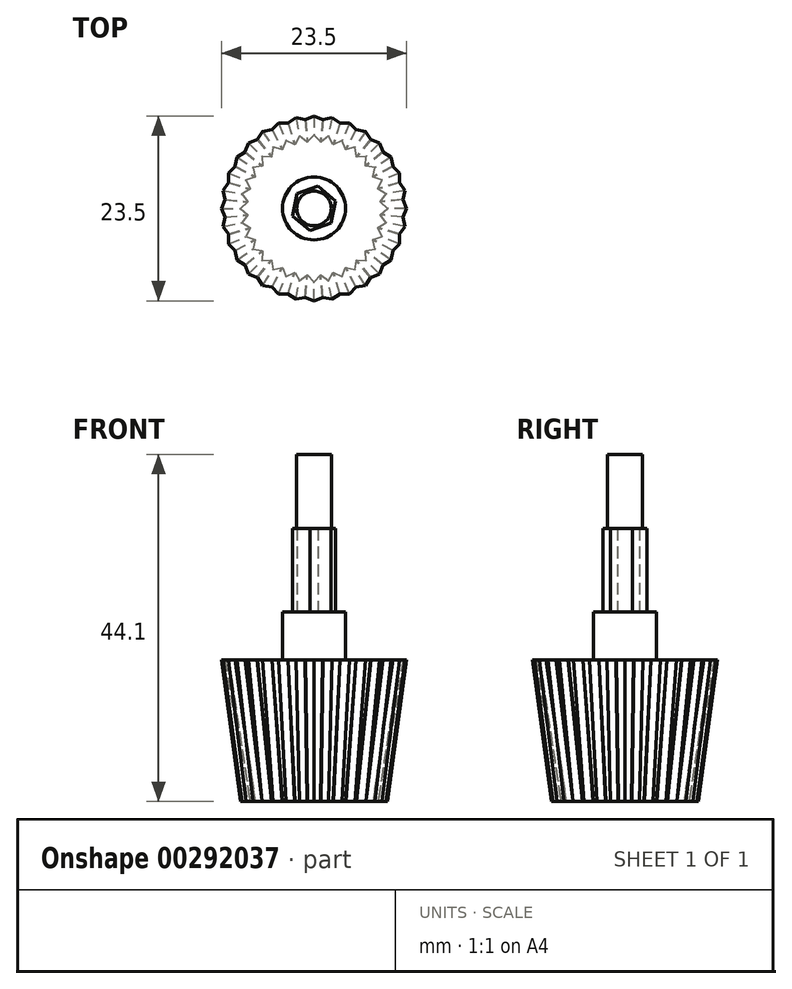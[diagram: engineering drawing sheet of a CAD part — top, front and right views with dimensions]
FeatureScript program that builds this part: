
annotation { "Feature Type Name" : "Feature", "Feature Type Description" : "" }
export const myFeature = defineFeature(function(context is Context, id is Id, definition is map)
    precondition{}
    {
        {
            var Q0;
            Q0=qCreatedBy(makeId("Top.planeOp"),FACE);
            var sketch = newSketch(context, id + "F0", { "sketchPlane" : qUnion([Q0])});
            skCircle(sketch, "E0", {"center": v(0, 0) * mm, "radius": 8.5 * mm});
            skSolve(sketch);
        }
        {
            var Q0;
            Q0 = qSketchRegion(id + "F0", true);
            extrude(context, id + "F1", {"entities" : qUnion([Q0]), "depth" : 18 * mm, "hasDraft" : true, "draftAngle" : 9 * degree});
        }
        {
            var Q0;
            Q0=makeQuery(id+"F1.opExtrude","CAP_FACE",FACE,{"disambiguationData":[OSD([sQuery(id+"F0.wireOp",EDGE,"E0")])],"isStart":false});
            var sketch = newSketch(context, id + "F2", { "sketchPlane" : qUnion([Q0])});
            skLineSegment(sketch, "E1", {"start": v(-1.1, 11.3) * mm, "end": v(0, 11.75) * mm});
            skLineSegment(sketch, "E2", {"start": v(0, 11.75) * mm, "end": v(1.1, 11.3) * mm});
            skLineSegment(sketch, "E3", {"start": v(1.1, 11.3) * mm, "end": v(-1.1, 11.3) * mm});
            skSolve(sketch);
        }
        {
            var Q0;
            Q0=makeQuery(id+"F1.opExtrude","CAP_FACE",FACE,{"disambiguationData":[OSD([sQuery(id+"F0.wireOp",EDGE,"E0")])],"isStart":true});
            var sketch = newSketch(context, id + "F3", { "sketchPlane" : qUnion([Q0])});
            skLineSegment(sketch, "E4", {"start": v(0.8, -8.46) * mm, "end": v(0, -9.34) * mm});
            skLineSegment(sketch, "E5", {"start": v(0, -9.34) * mm, "end": v(-0.8, -8.46) * mm});
            skLineSegment(sketch, "E6", {"start": v(-0.8, -8.46) * mm, "end": v(0.8, -8.46) * mm});
            skSolve(sketch);
        }
        {
            var Q0;
            Q0 = qSketchRegion(id + "F2", true);
            var Q1;
            Q1 = qSketchRegion(id + "F3", true);
            var Q2;
            {var subQ0=sQuery(id+"F2.wireOp",EDGE,"E1");Q2=makeQuery(id+"F2.imprint","IMPRINT",FACE,{"disambiguationData":[TD([[makeQuery(id+"F2.imprint","IMPRINT",EDGE,{"derivedFrom":subQ0}),-1.0]])]});}
            var Q3;
            {var subQ0=sQuery(id+"F3.wireOp",EDGE,"E4");Q3=makeQuery(id+"F3.imprint","IMPRINT",FACE,{"disambiguationData":[TD([[makeQuery(id+"F3.imprint","IMPRINT",EDGE,{"derivedFrom":subQ0}),-1.0]])]});}
            loft(context, id + "F4", {"sheetProfilesArray" : [{ "sheetProfileEntities" : qUnion([Q0]) }, { "sheetProfileEntities" : qUnion([Q1]) }], "wireProfilesArray" : [{ "wireProfileEntities" : qUnion([Q2]) }, { "wireProfileEntities" : qUnion([Q3]) }]});
        }
        {
            var Q0;
            {var subQ0=sQuery(id+"F3.wireOp",EDGE,"E4");var subQ5=sQuery(id+"F2.wireOp",EDGE,"E1");Q0=makeQuery(id+"F4.opLoft","SWEPT_BODY",BODY,{"disambiguationData":[OSD([makeQuery(id+"F2.imprint","IMPRINT",FACE,{"disambiguationData":[TD([[makeQuery(id+"F2.imprint","IMPRINT",EDGE,{"derivedFrom":subQ5}),-1.0]])]}),makeQuery(id+"F3.imprint","IMPRINT",FACE,{"disambiguationData":[TD([[makeQuery(id+"F3.imprint","IMPRINT",EDGE,{"derivedFrom":subQ0}),-1.0]])]})])]});}
            var Q1;
            Q1=makeQuery(id+"F1.opExtrude","CAP_EDGE",EDGE,{"disambiguationData":[OSD([sQuery(id+"F0.wireOp",EDGE,"E0")])],"isStart":true});
            circularPattern(context, id + "F5", {"operationType" : NewBodyOperationType.ADD, "entities" : qUnion([Q0]), "axis" : qUnion([Q1]), "angle" : 360 * degree, "instanceCount" : 32, "equalSpace" : true});
        }
        {
            var Q0;
            {var subQ0=sQuery(id+"F2.wireOp",EDGE,"E3");var subQ1=sQuery(id+"F0.wireOp",EDGE,"E0");var subQ3=makeQuery(id+"F4.opLoft","CAP_FACE",FACE,{"disambiguationData":[OSD([makeQuery(id+"F2.imprint","IMPRINT",FACE,{"disambiguationData":[TD([[makeQuery(id+"F2.imprint","IMPRINT",EDGE,{"derivedFrom":subQ0}),-1.0]])]})])],"isStart":true});Q0=makeQuery(id+"F5.boolean.opBoolean","MERGE",FACE,{"derivedFrom":[makeQuery(id+"F1.opExtrude","CAP_FACE",FACE,{"disambiguationData":[OSD([subQ1])],"isStart":false}),subQ3,makeQuery(id+"F5.opPattern","COPY",FACE,{"derivedFrom":subQ3,"instanceName":"1"}),makeQuery(id+"F5.opPattern","COPY",FACE,{"derivedFrom":subQ3,"instanceName":"2"}),makeQuery(id+"F5.opPattern","COPY",FACE,{"derivedFrom":subQ3,"instanceName":"3"}),makeQuery(id+"F5.opPattern","COPY",FACE,{"derivedFrom":subQ3,"instanceName":"4"}),makeQuery(id+"F5.opPattern","COPY",FACE,{"derivedFrom":subQ3,"instanceName":"5"}),makeQuery(id+"F5.opPattern","COPY",FACE,{"derivedFrom":subQ3,"instanceName":"6"}),makeQuery(id+"F5.opPattern","COPY",FACE,{"derivedFrom":subQ3,"instanceName":"7"}),makeQuery(id+"F5.opPattern","COPY",FACE,{"derivedFrom":subQ3,"instanceName":"8"}),makeQuery(id+"F5.opPattern","COPY",FACE,{"derivedFrom":subQ3,"instanceName":"9"}),makeQuery(id+"F5.opPattern","COPY",FACE,{"derivedFrom":subQ3,"instanceName":"10"}),makeQuery(id+"F5.opPattern","COPY",FACE,{"derivedFrom":subQ3,"instanceName":"11"}),makeQuery(id+"F5.opPattern","COPY",FACE,{"derivedFrom":subQ3,"instanceName":"12"}),makeQuery(id+"F5.opPattern","COPY",FACE,{"derivedFrom":subQ3,"instanceName":"13"}),makeQuery(id+"F5.opPattern","COPY",FACE,{"derivedFrom":subQ3,"instanceName":"14"}),makeQuery(id+"F5.opPattern","COPY",FACE,{"derivedFrom":subQ3,"instanceName":"15"}),makeQuery(id+"F5.opPattern","COPY",FACE,{"derivedFrom":subQ3,"instanceName":"16"}),makeQuery(id+"F5.opPattern","COPY",FACE,{"derivedFrom":subQ3,"instanceName":"17"}),makeQuery(id+"F5.opPattern","COPY",FACE,{"derivedFrom":subQ3,"instanceName":"18"}),makeQuery(id+"F5.opPattern","COPY",FACE,{"derivedFrom":subQ3,"instanceName":"19"}),makeQuery(id+"F5.opPattern","COPY",FACE,{"derivedFrom":subQ3,"instanceName":"20"}),makeQuery(id+"F5.opPattern","COPY",FACE,{"derivedFrom":subQ3,"instanceName":"21"}),makeQuery(id+"F5.opPattern","COPY",FACE,{"derivedFrom":subQ3,"instanceName":"22"}),makeQuery(id+"F5.opPattern","COPY",FACE,{"derivedFrom":subQ3,"instanceName":"23"}),makeQuery(id+"F5.opPattern","COPY",FACE,{"derivedFrom":subQ3,"instanceName":"24"}),makeQuery(id+"F5.opPattern","COPY",FACE,{"derivedFrom":subQ3,"instanceName":"25"}),makeQuery(id+"F5.opPattern","COPY",FACE,{"derivedFrom":subQ3,"instanceName":"26"}),makeQuery(id+"F5.opPattern","COPY",FACE,{"derivedFrom":subQ3,"instanceName":"27"}),makeQuery(id+"F5.opPattern","COPY",FACE,{"derivedFrom":subQ3,"instanceName":"28"}),makeQuery(id+"F5.opPattern","COPY",FACE,{"derivedFrom":subQ3,"instanceName":"29"}),makeQuery(id+"F5.opPattern","COPY",FACE,{"derivedFrom":subQ3,"instanceName":"30"}),makeQuery(id+"F5.opPattern","COPY",FACE,{"derivedFrom":subQ3,"instanceName":"31"})]});}
            var sketch = newSketch(context, id + "F6", { "sketchPlane" : qUnion([Q0])});
            skCircle(sketch, "E7", {"center": v(0, 0) * mm, "radius": 4 * mm});
            skSolve(sketch);
        }
        {
            var Q0;
            Q0 = qSketchRegion(id + "F6", true);
            extrude(context, id + "F7", {"entities" : qUnion([Q0]), "operationType" : NewBodyOperationType.ADD, "depth" : 6.1 * mm});
        }
        {
            var Q0;
            Q0=makeQuery(id+"F7.opExtrude","CAP_FACE",FACE,{"disambiguationData":[OSD([sQuery(id+"F6.wireOp",EDGE,"E7")])],"isStart":false});
            var sketch = newSketch(context, id + "F8", { "sketchPlane" : qUnion([Q0])});
            skCircle(sketch, "E8.cCircle", {"center": v(0, 0) * mm, "radius": 2.49 * mm, "construction": true});
            skLineSegment(sketch, "E8.0", {"start": v(2.18, -1.87) * mm, "end": v(-0.53, -2.82) * mm});
            skLineSegment(sketch, "E8.1", {"start": v(-0.53, -2.82) * mm, "end": v(-2.7, -0.95) * mm});
            skLineSegment(sketch, "E8.2", {"start": v(-2.7, -0.95) * mm, "end": v(-2.18, 1.87) * mm});
            skLineSegment(sketch, "E8.3", {"start": v(-2.18, 1.87) * mm, "end": v(0.53, 2.82) * mm});
            skLineSegment(sketch, "E8.4", {"start": v(0.53, 2.82) * mm, "end": v(2.7, 0.95) * mm});
            skLineSegment(sketch, "E8.5", {"start": v(2.7, 0.95) * mm, "end": v(2.18, -1.87) * mm});
            skPoint(sketch, "E8.0.midPoint", {"position": v(0.82, -2.35) * mm});
            skSolve(sketch);
        }
        {
            var Q0;
            Q0 = qSketchRegion(id + "F8", true);
            extrude(context, id + "F9", {"entities" : qUnion([Q0]), "operationType" : NewBodyOperationType.ADD, "depth" : 10.6 * mm});
        }
        {
            var Q0;
            Q0=makeQuery(id+"F9.opExtrude","CAP_FACE",FACE,{"disambiguationData":[OSD([sQuery(id+"F8.wireOp",EDGE,"E8.0"),sQuery(id+"F8.wireOp",EDGE,"E8.1"),sQuery(id+"F8.wireOp",EDGE,"E8.2"),sQuery(id+"F8.wireOp",EDGE,"E8.3"),sQuery(id+"F8.wireOp",EDGE,"E8.4"),sQuery(id+"F8.wireOp",EDGE,"E8.5")])],"isStart":false});
            var sketch = newSketch(context, id + "F10", { "sketchPlane" : qUnion([Q0])});
            skCircle(sketch, "E9", {"center": v(0, 0) * mm, "radius": 2.2 * mm});
            skSolve(sketch);
        }
        {
            var Q0;
            Q0 = qSketchRegion(id + "F10", true);
            extrude(context, id + "F11", {"entities" : qUnion([Q0]), "operationType" : NewBodyOperationType.ADD, "depth" : 9.4 * mm});
        }
    });
